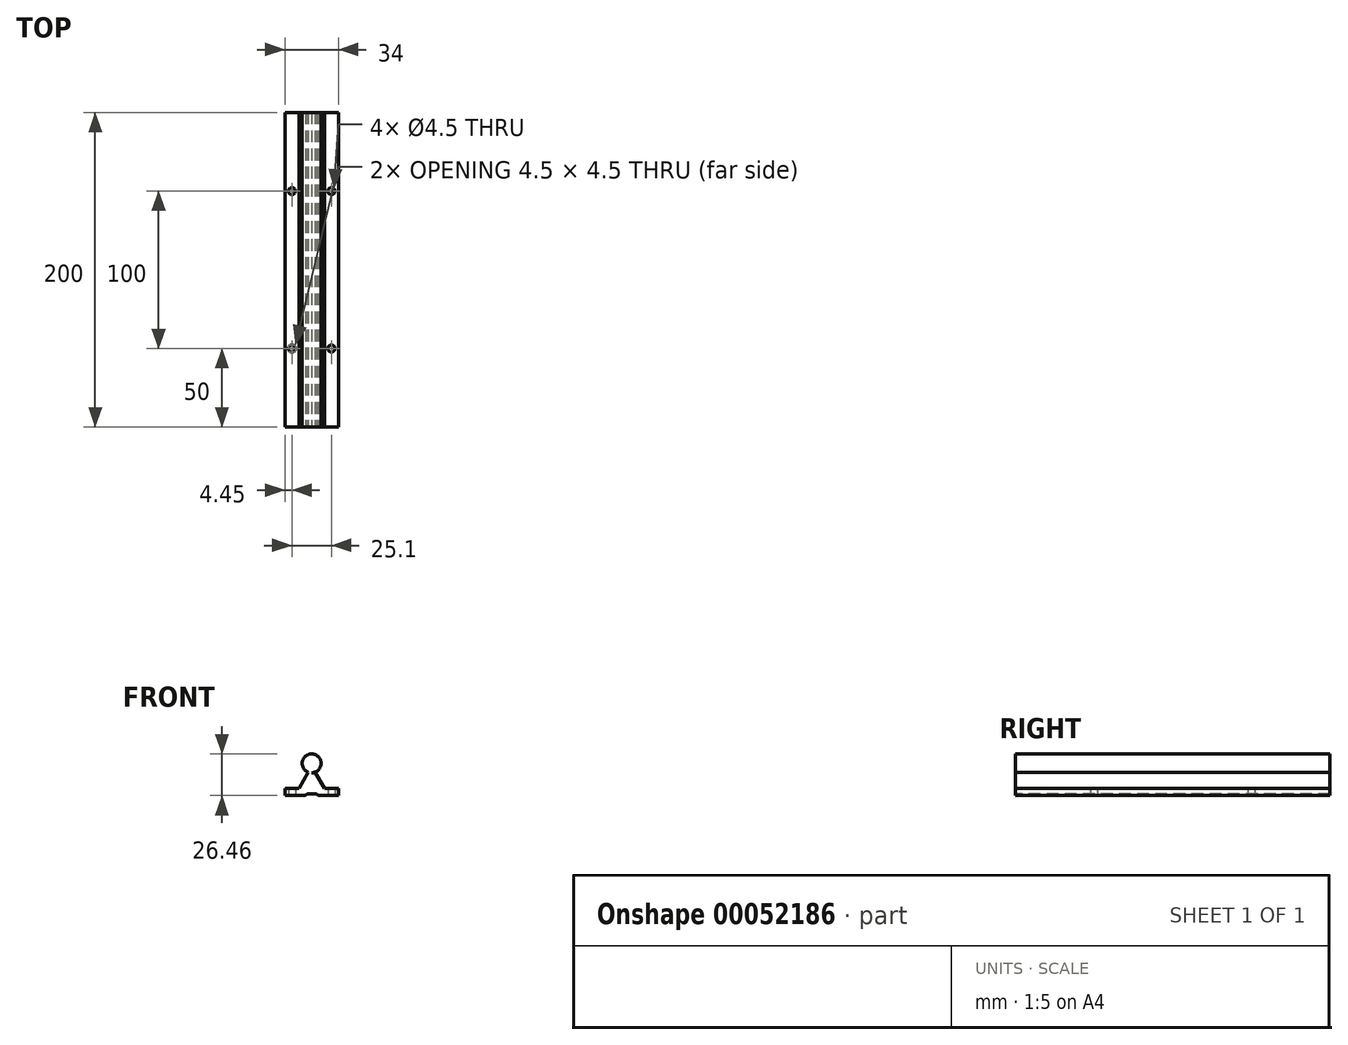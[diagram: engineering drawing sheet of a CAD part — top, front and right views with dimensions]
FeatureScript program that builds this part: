
annotation { "Feature Type Name" : "Feature", "Feature Type Description" : "" }
export const myFeature = defineFeature(function(context is Context, id is Id, definition is map)
    precondition{}
    {
        {
            var Q0;
            Q0=qCreatedBy(makeId("Front.planeOp"),FACE);
            var sketch = newSketch(context, id + "F0", { "sketchPlane" : qUnion([Q0])});
            skLineSegment(sketch, "E0", {"start": v(4, -1) * mm, "end": v(17, -1) * mm, "construction": true});
            skLineSegment(sketch, "E1", {"start": v(17, -1) * mm, "end": v(17, 3.5) * mm, "construction": true});
            skLineSegment(sketch, "E2", {"start": v(17, 3.5) * mm, "end": v(8.1, 3.5) * mm, "construction": true});
            skLineSegment(sketch, "E3", {"start": v(0, 0) * mm, "end": v(0.04, 19.46) * mm, "construction": true});
            skArc(sketch, "E4", {"start": v(0.03, 13.46) * mm, "mid": v(1.1, 13.56) * mm, "end": v(2.15, 13.85) * mm});
            skLineSegment(sketch, "E5", {"start": v(8.1, 3.5) * mm, "end": v(2.15, 13.85) * mm});
            skLineSegment(sketch, "E6", {"start": v(4, -1) * mm, "end": v(17, -1) * mm});
            skLineSegment(sketch, "E7", {"start": v(3, 0) * mm, "end": v(4, -1) * mm});
            skLineSegment(sketch, "E8", {"start": v(17, -1) * mm, "end": v(17, 3.5) * mm});
            skLineSegment(sketch, "E9", {"start": v(8.1, 3.5) * mm, "end": v(17, 3.5) * mm});
            skLineSegment(sketch, "E10", {"start": v(3, 0) * mm, "end": v(0, 0) * mm});
            skArc(sketch, "E11", {"start": v(2.15, 13.85) * mm, "mid": v(1.1, 13.56) * mm, "end": v(0.03, 13.46) * mm});
            skArc(sketch, "E12.MirrorCS", {"start": v(-2.1, 13.85) * mm, "mid": v(-1.05, 13.56) * mm, "end": v(0.03, 13.46) * mm});
            skLineSegment(sketch, "E13.MirrorCS", {"start": v(-8.09, 3.53) * mm, "end": v(-2.1, 13.85) * mm});
            skLineSegment(sketch, "E14.MirrorCS", {"start": v(-8.09, 3.53) * mm, "end": v(-16.99, 3.57) * mm});
            skLineSegment(sketch, "E15.MirrorCS", {"start": v(-17, -0.93) * mm, "end": v(-16.99, 3.57) * mm});
            skLineSegment(sketch, "E16.MirrorCS", {"start": v(-4, -0.98) * mm, "end": v(-17, -0.93) * mm});
            skLineSegment(sketch, "E17.MirrorCS", {"start": v(-3, 0.01) * mm, "end": v(-4, -0.98) * mm});
            skLineSegment(sketch, "E18.MirrorCS", {"start": v(-3, 0.01) * mm, "end": v(0, 0) * mm});
            skSolve(sketch);
        }
        {
            var Q0;
            Q0 = qSketchRegion(id + "F0", true);
            extrude(context, id + "F1", {"entities" : qUnion([Q0]), "oppositeDirection" : true, "depth" : 200 * mm});
        }
        {
            var Q0;
            Q0=qCreatedBy(makeId("Front.planeOp"),FACE);
            var sketch = newSketch(context, id + "F2", { "sketchPlane" : qUnion([Q0])});
            skCircle(sketch, "E19", {"center": v(0, 19.46) * mm, "radius": 6 * mm});
            skSolve(sketch);
        }
        {
            var Q0;
            Q0=makeQuery(id+"F2.imprint","IMPRINT",FACE,{"disambiguationData":[TD([[makeQuery(id+"F2.imprint","IMPRINT",EDGE,{"derivedFrom":sQuery(id+"F2.wireOp",EDGE,"E19")}),1.0]])]});
            extrude(context, id + "F3", {"entities" : qUnion([Q0]), "operationType" : NewBodyOperationType.ADD, "oppositeDirection" : true, "depth" : 200 * mm});
        }
        {
            var Q0;
            Q0=makeQuery(id+"F1.opExtrude","SWEPT_FACE",FACE,{"disambiguationData":[OSD([sQuery(id+"F0.wireOp",EDGE,"E6")])]});
            var sketch = newSketch(context, id + "F4", { "sketchPlane" : qUnion([Q0])});
            skLineSegment(sketch, "E20", {"start": v(17, 0) * mm, "end": v(12.55, 0) * mm, "construction": true});
            skLineSegment(sketch, "E21", {"start": v(12.55, 0) * mm, "end": v(12.55, -50) * mm, "construction": true});
            skLineSegment(sketch, "E22", {"start": v(12.55, -50) * mm, "end": v(12.55, -150) * mm, "construction": true});
            skCircle(sketch, "E23", {"center": v(12.55, -50) * mm, "radius": 2.25 * mm});
            skCircle(sketch, "E24", {"center": v(12.55, -150) * mm, "radius": 2.25 * mm});
            skLineSegment(sketch, "E25", {"start": v(0, -4) * mm, "end": v(0, -215.87) * mm, "construction": true});
            skCircle(sketch, "E26.MirrorC", {"center": v(-12.55, -150) * mm, "radius": 2.25 * mm});
            skCircle(sketch, "E27.MirrorC", {"center": v(-12.55, -50) * mm, "radius": 2.25 * mm});
            skSolve(sketch);
        }
        {
            var Q0;
            Q0 = qSketchRegion(id + "F4", true);
            extrude(context, id + "F5", {"entities" : qUnion([Q0]), "operationType" : NewBodyOperationType.REMOVE, "endBound" : BoundingType.THROUGH_ALL, "oppositeDirection" : true, "depth" : 25 * mm});
        }
    });
